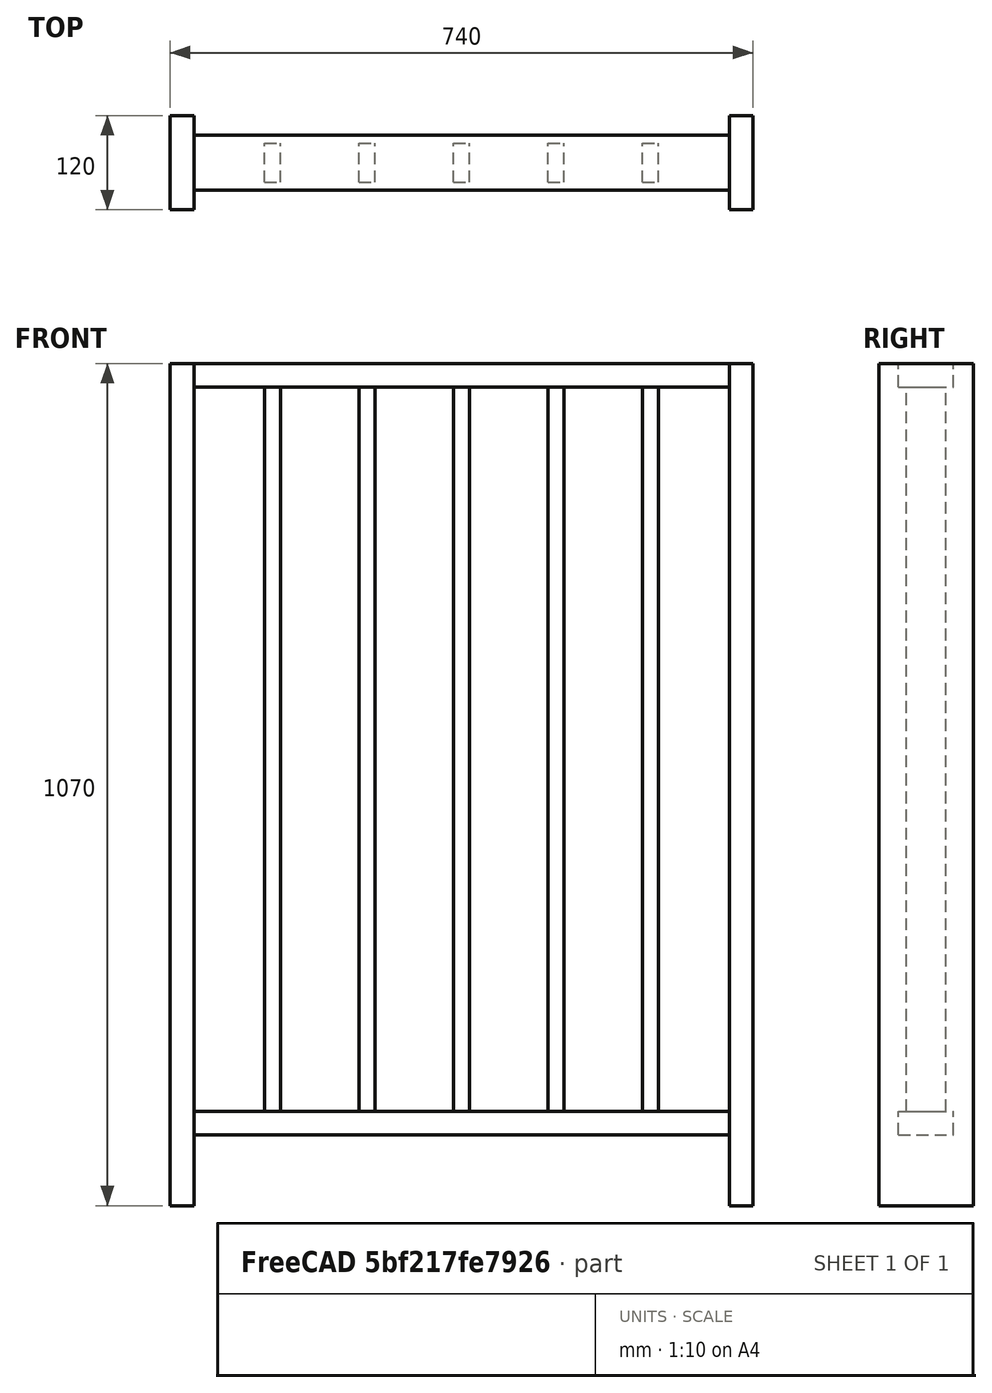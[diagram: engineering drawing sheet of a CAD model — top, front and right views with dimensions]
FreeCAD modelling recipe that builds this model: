
FCSTD DOCUMENT  (FreeCAD 0.18R16146 (Git))
Label: guarda-corpo-grade-modulo-3
License: All rights reserved
LicenseURL: http://en.wikipedia.org/wiki/All_rights_reserved
objects: Part::Box×5, Spreadsheet::Sheet×1, Part::FeaturePython×1, Part::Compound×1, Part::Feature×1
note: 8 computed .brp shape members not serialized (recipe doc carries the construction recipe); baked Part::Feature solids carry a one-line shape summary decoded from their .brp

FEATURE [Spreadsheet::Sheet] Spreadsheet  label="medidas"
  cells = B1=altura (height); C1=frente (length); D1=profundidade (width); E1=z; F1=x; G1=y; H1=quantidade; A2=pe_direito_1; B2(pe_direito_1_height)=1070; C2(pe_direito_1_length)=30; D2(pe_direito_1_width)=120; E2(pe_direito_1_z)=0; F2(pe_direito_1_x)=0; G2(pe_direito_1_y)=0; H2=1; A3=pe_direito_2; B3(pe_direito_2_height)=1070; C3(pe_direito_2_length)=30; D3(pe_direito_2_width)=120; E3(pe_direito_2_z)=0; F3(pe_direito_2_x)=710; G3(pe_direito_2_y)=0; H3=1; A4=travessa_inferior; B4(travessa_inferior_height)=30; C4(travessa_inferior_length)=680; D4(travessa_inferior_width)=70; E4(travessa_inferior_z)=90; F4(travessa_inferior_x)=30; G4(travessa_inferior_y)=25; H4=1; A5=travessa_superior; B5(travessa_superior_height)=30; C5(travessa_superior_length)=680; D5(travessa_superior_width)=70; E5(travessa_superior_z)=1040; F5(travessa_superior_x)=30; G5(travessa_superior_y)=25; H5=1; A6=palito_grade; B6(palito_grade_height)=920; C6(palito_grade_length)=20; D6(palito_grade_width)=50; E6(palito_grade_z)=0; F6(palito_grade_x)=0; G6(palito_grade_y)=0; H6=1; A7=palitos; C7(palitos_length)=120; E7(palitos_z)=120; F7(palitos_x)=120; G7(palitos_y)=35; H7(palitos_qty)=5
FEATURE [Part::Box] Box  label="pe_direito_1"
  AttacherType = Attacher::AttachEngine3D
  Height = 1070
  Length = 30
  Width = 120
  expr: Placement.Base.z = medidas.pe_direito_1_z
  expr: Placement.Base.y = medidas.pe_direito_1_y
  expr: Placement.Base.x = medidas.pe_direito_1_x
  expr: Height = medidas.pe_direito_1_height
  expr: Width = medidas.pe_direito_1_width
  expr: Length = medidas.pe_direito_1_length
FEATURE [Part::Box] Box001  label="pe_direito_2"
  AttacherType = Attacher::AttachEngine3D
  Height = 1070
  Length = 30
  Placement = pos=(710,0,0) rot=(0,0,1;0rad)
  Width = 120
  expr: Placement.Base.z = medidas.pe_direito_2_z
  expr: Placement.Base.y = medidas.pe_direito_2_y
  expr: Placement.Base.x = medidas.pe_direito_2_x
  expr: Height = medidas.pe_direito_2_height
  expr: Width = medidas.pe_direito_2_width
  expr: Length = medidas.pe_direito_2_length
FEATURE [Part::Box] Box002  label="travessa_inferior"
  AttacherType = Attacher::AttachEngine3D
  Height = 30
  Length = 680
  Placement = pos=(30,25,90) rot=(0,0,1;0rad)
  Width = 70
  expr: Placement.Base.z = medidas.travessa_inferior_z
  expr: Placement.Base.y = medidas.travessa_inferior_y
  expr: Placement.Base.x = medidas.travessa_inferior_x
  expr: Height = medidas.travessa_inferior_height
  expr: Width = medidas.travessa_inferior_width
  expr: Length = medidas.travessa_inferior_length
FEATURE [Part::Box] Box003  label="travessa_superior"
  AttacherType = Attacher::AttachEngine3D
  Height = 30
  Length = 680
  Placement = pos=(30,25,1040) rot=(0,0,1;0rad)
  Width = 70
  expr: Placement.Base.z = medidas.travessa_superior_z
  expr: Placement.Base.y = medidas.travessa_superior_y
  expr: Placement.Base.x = medidas.travessa_superior_x
  expr: Height = medidas.travessa_superior_height
  expr: Width = medidas.travessa_superior_width
  expr: Length = medidas.travessa_superior_length
FEATURE [Part::Box] Box004  label="palito_grade"
  AttacherType = Attacher::AttachEngine3D
  Height = 920
  Length = 20
  Width = 50
  expr: Placement.Base.z = medidas.palito_grade_z
  expr: Placement.Base.y = medidas.palito_grade_y
  expr: Placement.Base.x = medidas.palito_grade_x
  expr: Height = medidas.palito_grade_height
  expr: Width = medidas.palito_grade_width
  expr: Length = medidas.palito_grade_length
FEATURE [Part::FeaturePython] Array  label="palitos"  # Draft array (typed FeaturePython)
  Angle = 360
  ArrayType = 0
  Axis = (0,0,1)
  Base = -> Box004
  Center = (0,0,0)
  Fuse = false
  IntervalAxis = (0,0,0)
  IntervalX = (120,0,0)
  IntervalY = (0,1,0)
  IntervalZ = (0,0,1)
  NumberPolar = 1
  NumberX = 5
  NumberY = 1
  NumberZ = 1
  Placement = pos=(120,35,120) rot=(0,0,1;0rad)
  expr: IntervalX.x = medidas.palitos_length
  expr: NumberX = medidas.palitos_qty
  expr: Placement.Base.z = medidas.palitos_z
  expr: Placement.Base.y = medidas.palitos_y
  expr: Placement.Base.x = medidas.palitos_x
FEATURE [Part::Compound] Compound  label="modulo_3"
  Links = -> [Box,Box001,Box002,Box003,Array]
FEATURE [Part::Feature] Compound001  label="modulo_3_copy"
  shape: bbox 740 x 120 x 1070 mm, 54 faces, 9 solids (baked)
